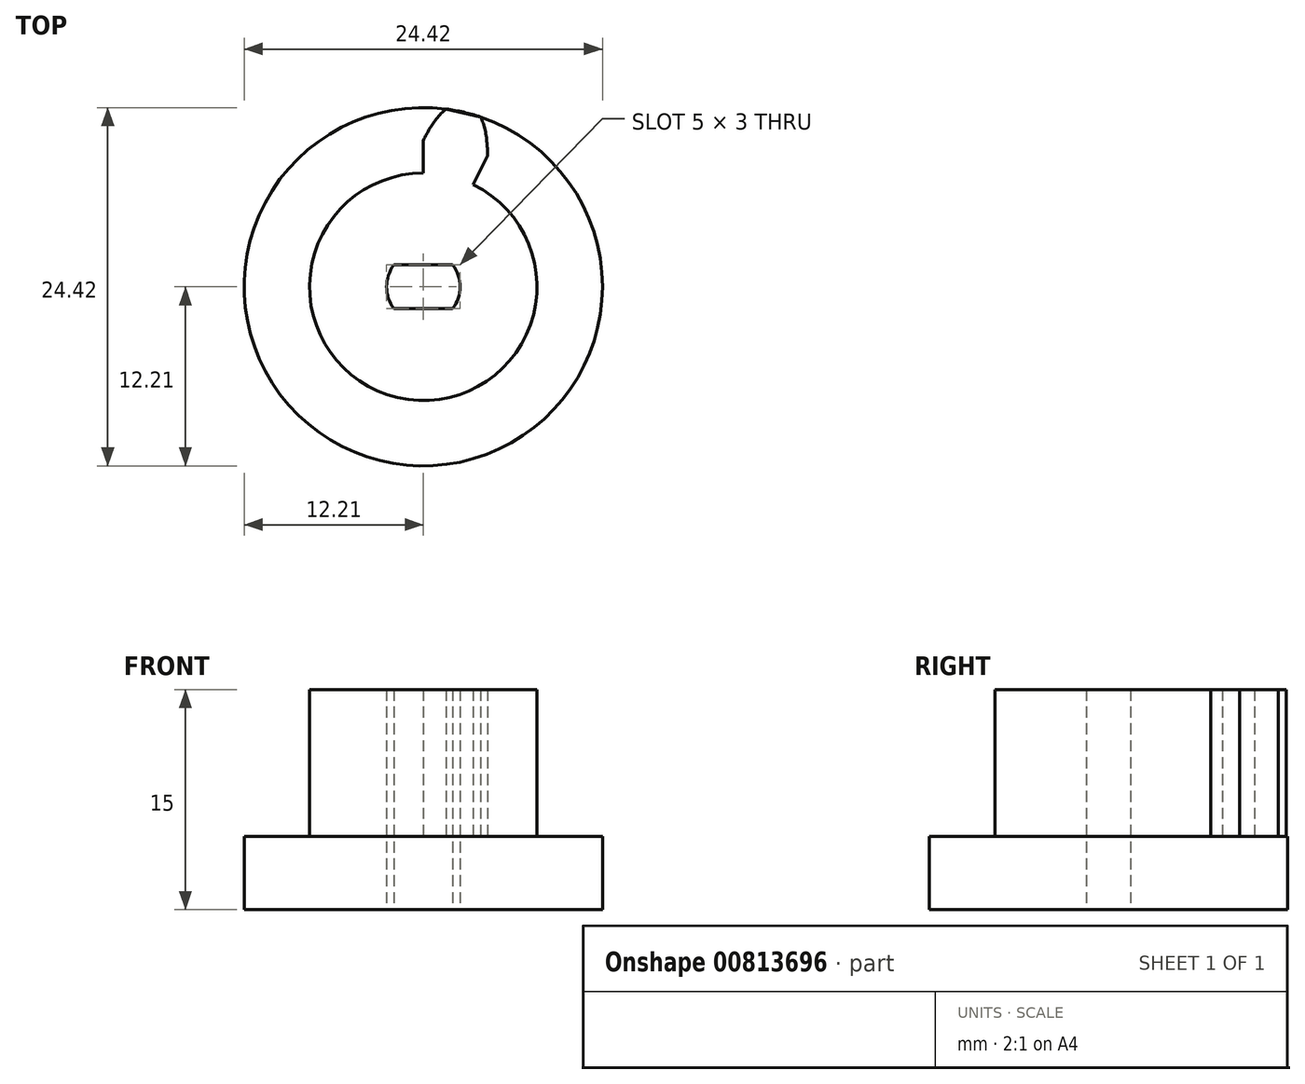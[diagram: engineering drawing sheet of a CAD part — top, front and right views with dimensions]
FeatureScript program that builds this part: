
annotation { "Feature Type Name" : "Feature", "Feature Type Description" : "" }
export const myFeature = defineFeature(function(context is Context, id is Id, definition is map)
    precondition{}
    {
        {
            var Q0;
            Q0=qCreatedBy(makeId("Top.planeOp"),FACE);
            var sketch = newSketch(context, id + "F0", { "sketchPlane" : qUnion([Q0])});
            skArc(sketch, "E0", {"start": v(-2, 1.5) * mm, "mid": v(-2.5, 0) * mm, "end": v(-2, -1.5) * mm});
            skCircle(sketch, "E1", {"center": v(0, 0) * mm, "radius": 7.75 * mm});
            skLineSegment(sketch, "E2", {"start": v(-0.01, 7.75) * mm, "end": v(-0.01, 9.95) * mm});
            skLineSegment(sketch, "E3", {"start": v(1.56, 12.1) * mm, "end": v(3.9, 11.57) * mm});
            skFitSpline(sketch, "E4", {"points": [v(-0.01, 9.95) * mm, v(1.56, 12.1) * mm], "startDerivative": vector(0.84, 1.8) * mm, "endDerivative": vector(2.04, 1.47) * mm});
            skLineSegment(sketch, "E5", {"start": v(0, 0) * mm, "end": v(2.73, 11.84) * mm, "construction": true});
            skFitSpline(sketch, "E6.MirrorCS", {"points": [v(4.37, 8.94) * mm, v(3.9, 11.57) * mm], "startDerivative": vector(0.03, 2) * mm, "endDerivative": vector(-1.2, 2.22) * mm});
            skLineSegment(sketch, "E7.MirrorCS", {"start": v(3.4, 6.96) * mm, "end": v(4.37, 8.94) * mm});
            skLineSegment(sketch, "E8.1.0", {"start": v(-7.73, -0.53) * mm, "end": v(-9.93, -0.68) * mm});
            skLineSegment(sketch, "E8.2.0", {"start": v(4.32, -6.43) * mm, "end": v(5.55, -8.26) * mm});
            skArc(sketch, "E9", {"start": v(2, -1.5) * mm, "mid": v(2.5, 0) * mm, "end": v(2, 1.5) * mm});
            skLineSegment(sketch, "E10", {"start": v(-2, 1.5) * mm, "end": v(2, 1.5) * mm});
            skLineSegment(sketch, "E11", {"start": v(2, -1.5) * mm, "end": v(-2, -1.5) * mm});
            skSolve(sketch);
        }
        {
            var Q0;
            Q0=makeQuery(id+"F0.imprint","IMPRINT",FACE,{"disambiguationData":[TD([[makeQuery(id+"F0.imprint","IMPRINT",EDGE,{"derivedFrom":sQuery(id+"F0.wireOp",EDGE,"E10")}),1.0]])]});
            extrude(context, id + "F1", {"entities" : qUnion([Q0]), "depth" : 10 * mm, "offsetDistance" : 25 * mm});
        }
        {
            var Q0;
            {var subQ0=sQuery(id+"F0.wireOp",EDGE,"E2");Q0=makeQuery(id+"F0.imprint","IMPRINT",FACE,{"disambiguationData":[TD([[makeQuery(id+"F0.imprint","IMPRINT",EDGE,{"derivedFrom":subQ0}),-1.0]])]});}
            extrude(context, id + "F2", {"entities" : qUnion([Q0]), "operationType" : NewBodyOperationType.ADD, "depth" : 10 * mm, "offsetDistance" : 25 * mm});
        }
        {
            var Q0;
            Q0=qCreatedBy(makeId("Front.planeOp"),FACE);
            var sketch = newSketch(context, id + "F3", { "sketchPlane" : qUnion([Q0])});
            skLineSegment(sketch, "E12", {"start": v(0, 0) * mm, "end": v(0, 36.64) * mm, "construction": true});
            skSolve(sketch);
        }
        {
            var Q0;
            Q0=makeQuery(id+"F0.imprint","IMPRINT",FACE,{"disambiguationData":[TD([[makeQuery(id+"F0.imprint","IMPRINT",EDGE,{"derivedFrom":sQuery(id+"F0.wireOp",EDGE,"E10")}),1.0]])]});
            var sketch = newSketch(context, id + "F4", { "sketchPlane" : qUnion([Q0])});
            skCircle(sketch, "E13", {"center": v(0, 0) * mm, "radius": 12.2 * mm});
            skSolve(sketch);
        }
        {
            var Q0;
            Q0=makeQuery(id+"F4.imprint","IMPRINT",FACE,{"disambiguationData":[TD([[makeQuery(id+"F4.imprint","IMPRINT",EDGE,{"derivedFrom":sQuery(id+"F4.wireOp",EDGE,"E13")}),1.0]])]});
            var Q1;
            Q1=makeQuery(id+"F0.imprint","IMPRINT",FACE,{"disambiguationData":[TD([[makeQuery(id+"F0.imprint","IMPRINT",EDGE,{"derivedFrom":sQuery(id+"F0.wireOp",EDGE,"E10")}),1.0]])]});
            extrude(context, id + "F5", {"entities" : qUnion([Q0, Q1]), "operationType" : NewBodyOperationType.ADD, "oppositeDirection" : true, "depth" : 5 * mm, "offsetDistance" : 25 * mm});
        }
    });
